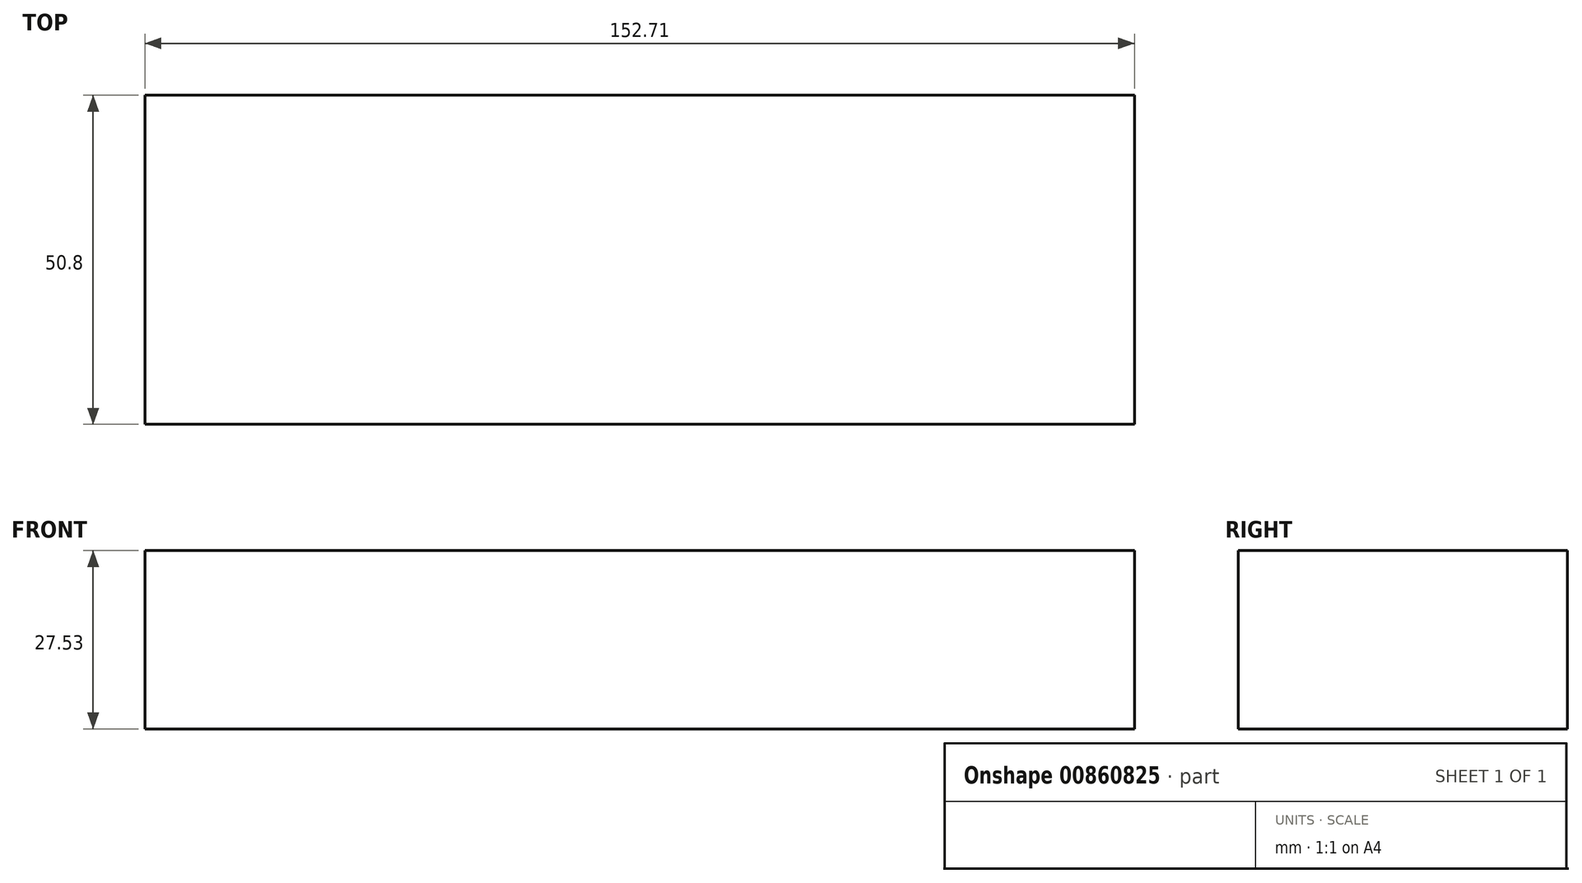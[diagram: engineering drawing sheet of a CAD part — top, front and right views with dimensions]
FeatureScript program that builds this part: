
annotation { "Feature Type Name" : "Feature", "Feature Type Description" : "" }
export const myFeature = defineFeature(function(context is Context, id is Id, definition is map)
    precondition{}
    {
        {
            var Q0;
            Q0=qCreatedBy(makeId("Front.planeOp"),FACE);
            var sketch = newSketch(context, id + "F0", { "sketchPlane" : qUnion([Q0])});
            skLineSegment(sketch, "E0", {"start": v(0, 0) * mm, "end": v(-152.7, 0) * mm});
            skLineSegment(sketch, "E1", {"start": v(-152.7, 0) * mm, "end": v(-152.7, 27.53) * mm});
            skLineSegment(sketch, "E2", {"start": v(-152.7, 27.53) * mm, "end": v(0, 27.53) * mm});
            skLineSegment(sketch, "E3", {"start": v(0, 27.53) * mm, "end": v(0, 0) * mm});
            skSolve(sketch);
        }
        {
            var Q0;
            Q0 = qSketchRegion(id + "F0", true);
            extrude(context, id + "F1", {"entities" : qUnion([Q0]), "depth" : 50.8 * mm, "offsetDistance" : 25.4 * mm});
        }
    });
